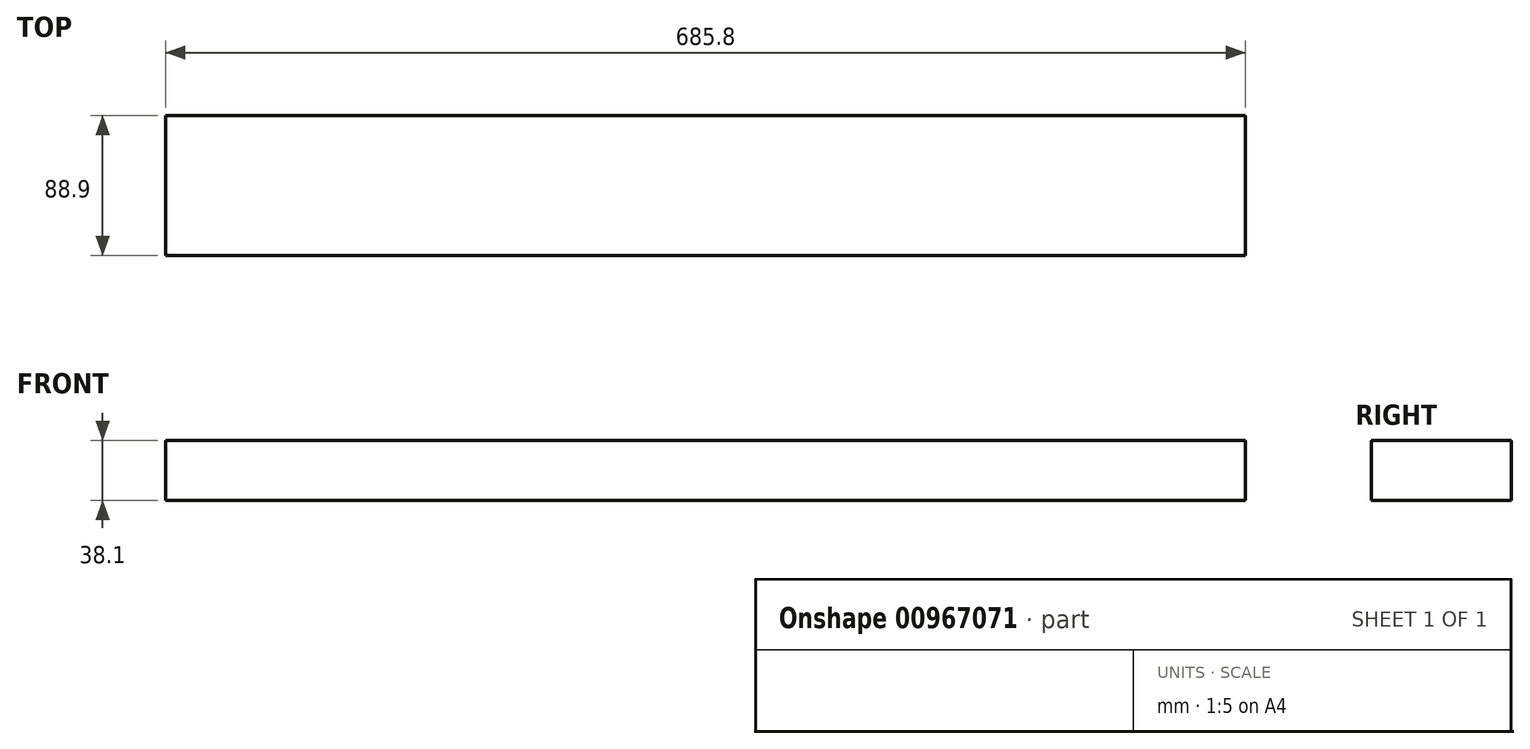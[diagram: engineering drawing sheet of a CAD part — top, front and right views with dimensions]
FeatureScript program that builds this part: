
annotation { "Feature Type Name" : "Feature", "Feature Type Description" : "" }
export const myFeature = defineFeature(function(context is Context, id is Id, definition is map)
    precondition{}
    {
        {
            var Q0;
            Q0=qCreatedBy(makeId("Right.planeOp"),FACE);
            var sketch = newSketch(context, id + "F0", { "sketchPlane" : qUnion([Q0])});
            skLineSegment(sketch, "E0.bottom", {"start": v(0, 0) * mm, "end": v(-88.9, 0) * mm});
            skLineSegment(sketch, "E0.top", {"start": v(0, 38.1) * mm, "end": v(-88.9, 38.1) * mm});
            skLineSegment(sketch, "E0.left", {"start": v(0, 0) * mm, "end": v(0, 38.1) * mm});
            skLineSegment(sketch, "E0.right", {"start": v(-88.9, 0) * mm, "end": v(-88.9, 38.1) * mm});
            skSolve(sketch);
        }
        {
            var Q0;
            Q0=makeQuery(id+"F0.imprint","IMPRINT",FACE,{"disambiguationData":[TD([[makeQuery(id+"F0.imprint","IMPRINT",EDGE,{"derivedFrom":sQuery(id+"F0.wireOp",EDGE,"E0.bottom")}),-1.0]])]});
            extrude(context, id + "F1", {"entities" : qUnion([Q0]), "oppositeDirection" : true, "depth" : 685.8 * mm, "offsetDistance" : 25.4 * mm});
        }
    });
